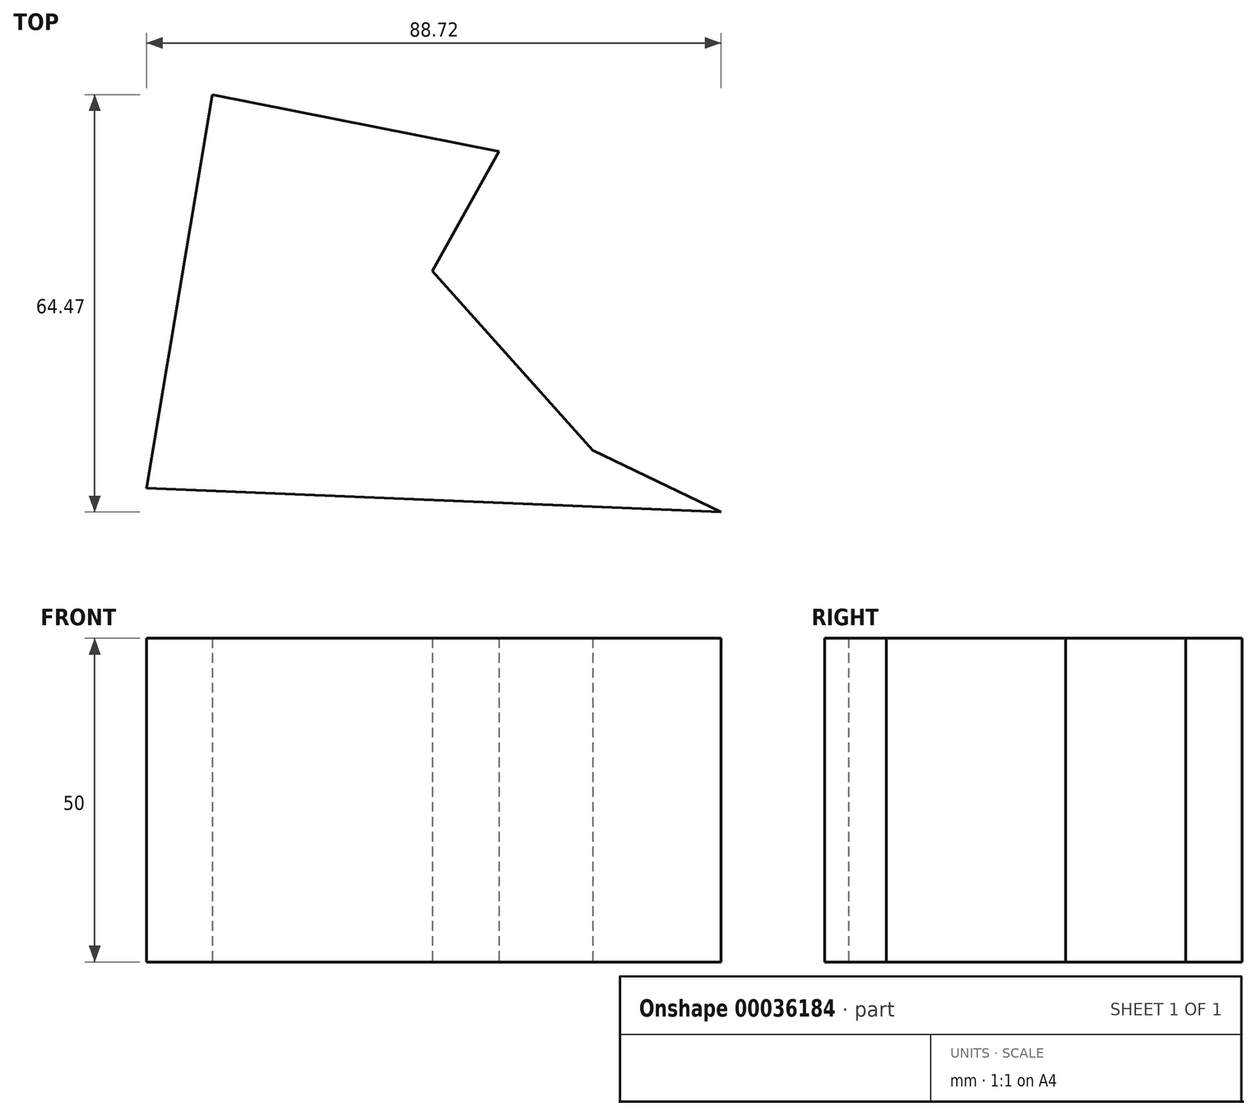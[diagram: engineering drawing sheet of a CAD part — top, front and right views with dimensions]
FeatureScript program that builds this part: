
annotation { "Feature Type Name" : "Feature", "Feature Type Description" : "" }
export const myFeature = defineFeature(function(context is Context, id is Id, definition is map)
    precondition{}
    {
        {
            var Q0;
            Q0=qCreatedBy(makeId("Top.planeOp"),FACE);
            var sketch = newSketch(context, id + "F0", { "sketchPlane" : qUnion([Q0])});
            skLineSegment(sketch, "E0", {"start": v(-29.62, 42.93) * mm, "end": v(14.66, 34.19) * mm});
            skLineSegment(sketch, "E1", {"start": v(14.66, 34.19) * mm, "end": v(4.34, 15.65) * mm});
            skLineSegment(sketch, "E2", {"start": v(4.34, 15.65) * mm, "end": v(29.14, -12) * mm});
            skLineSegment(sketch, "E3", {"start": v(29.14, -12) * mm, "end": v(48.94, -21.54) * mm});
            skLineSegment(sketch, "E4", {"start": v(48.94, -21.54) * mm, "end": v(-39.78, -17.87) * mm});
            skLineSegment(sketch, "E5", {"start": v(-39.78, -17.87) * mm, "end": v(-29.62, 42.93) * mm});
            skSolve(sketch);
        }
        {
            var Q0;
            Q0 = qSketchRegion(id + "F0", true);
            extrude(context, id + "F1", {"entities" : qUnion([Q0]), "depth" : 50 * mm});
        }
    });
